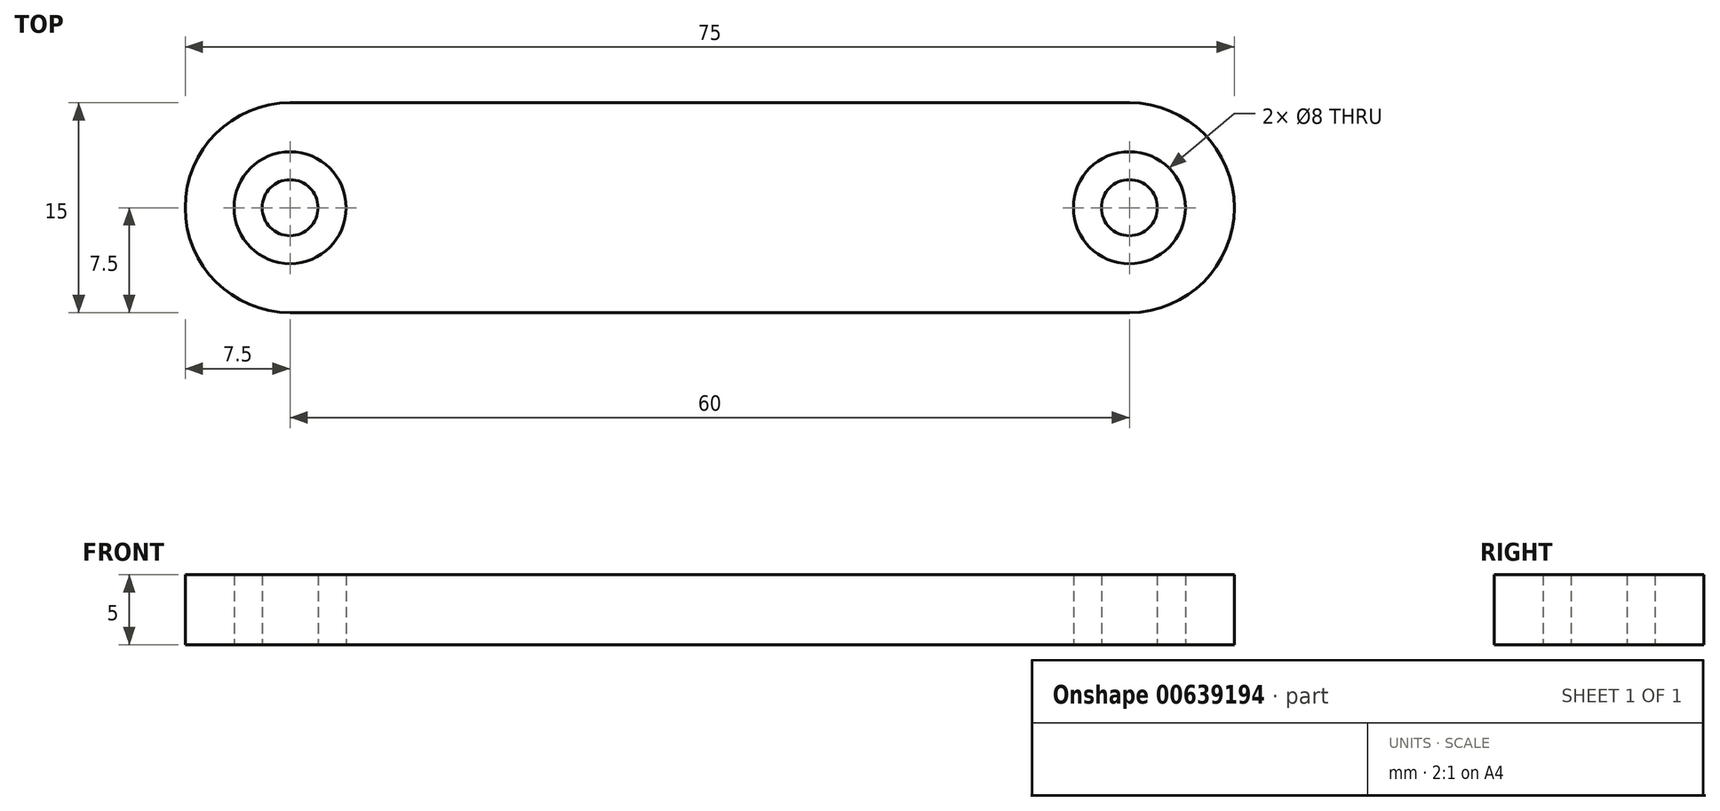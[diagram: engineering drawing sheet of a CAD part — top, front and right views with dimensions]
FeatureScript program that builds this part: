
annotation { "Feature Type Name" : "Feature", "Feature Type Description" : "" }
export const myFeature = defineFeature(function(context is Context, id is Id, definition is map)
    precondition{}
    {
        {
            var Q0;
            Q0=qCreatedBy(makeId("Top.planeOp"),FACE);
            var sketch = newSketch(context, id + "F0", { "sketchPlane" : qUnion([Q0])});
            skLineSegment(sketch, "E0", {"start": v(0, 0) * mm, "end": v(60, 0) * mm, "construction": true});
            skArc(sketch, "E1", {"start": v(0, 7.5) * mm, "mid": v(-7.5, 0) * mm, "end": v(0, -7.5) * mm});
            skArc(sketch, "E2", {"start": v(60, -7.5) * mm, "mid": v(67.5, 0) * mm, "end": v(60, 7.5) * mm});
            skLineSegment(sketch, "E3", {"start": v(0, 7.5) * mm, "end": v(60, 7.5) * mm});
            skLineSegment(sketch, "E4", {"start": v(0, -7.5) * mm, "end": v(60, -7.5) * mm});
            skCircle(sketch, "E5", {"center": v(0, 0) * mm, "radius": 4 * mm});
            skCircle(sketch, "E6", {"center": v(60, 0) * mm, "radius": 4 * mm});
            skSolve(sketch);
        }
        {
            var Q0;
            Q0 = qSketchRegion(id + "F0", true);
            extrude(context, id + "F1", {"entities" : qUnion([Q0]), "depth" : 5 * mm, "offsetDistance" : 25 * mm});
        }
        {
            var Q0;
            Q0=qCreatedBy(makeId("Top.planeOp"),FACE);
            var sketch = newSketch(context, id + "F2", { "sketchPlane" : qUnion([Q0])});
            skCircle(sketch, "E7", {"center": v(0, 0) * mm, "radius": 2 * mm});
            skCircle(sketch, "E8", {"center": v(60, 0) * mm, "radius": 2 * mm});
            skSolve(sketch);
        }
        {
            var Q0;
            Q0 = qSketchRegion(id + "F2", true);
            extrude(context, id + "F3", {"entities" : qUnion([Q0]), "depth" : 5 * mm, "offsetDistance" : 25 * mm});
        }
    });
